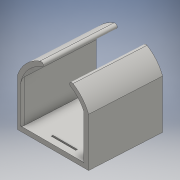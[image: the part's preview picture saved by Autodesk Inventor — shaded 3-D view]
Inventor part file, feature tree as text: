
AUTODESK INVENTOR PART (.ipt)
format: ipt  version: 2016 (Build 200138000, 138)  size: 526,336 bytes
history: native  units: in
note: dims shown in document units (in); Inventor stores cm internally (conversion verified against a paired STEP export)
features: sketch x3, sweep x1, hole x1, pattern_linear x1, fillet x1, split x1
ambient origin geometry x8: Origin, YZ Plane, XZ Plane, XY Plane, X Axis, Y Axis, Z Axis, Center Point
bodies: Body1 (feature_tree)
feature tree (8):
  sweep  "Sweep4"
  hole  "Hole3"  [1 undecoded]
  pattern_linear  "Rectangular Pattern3"  Spacing1=0.3in  [1 undecoded]
  fillet  "Fillet7"  Radius=0.3in
  split  "Split8"
  sketch  "Sketch17"  dims[d137=3.122in d143=3.75in]
  sketch  "Sketch21"  dims[d151=4.5in d152=0.25in]
  sketch  "Sketch24"  dims[d153=0.0in d154=0.0in d175=0.3in d176=0.3in d178=0.3in d188=1.0in d189=1.0in d181=0.1575in d182=0.75in d183=0.375in d184=0.25in d185=0.5635in d186=1.0in d187=0.8108in d190=2.3622in d192=0.629in d193=0.125in d34=1.0in d35=1.0in d80=1.0in d81=1.0in]
note: 2 required parameter values undecoded (feature->parameter linkage not recoverable at this tier; creation-order binding heuristic only, values carry confidence <= 0.55)
